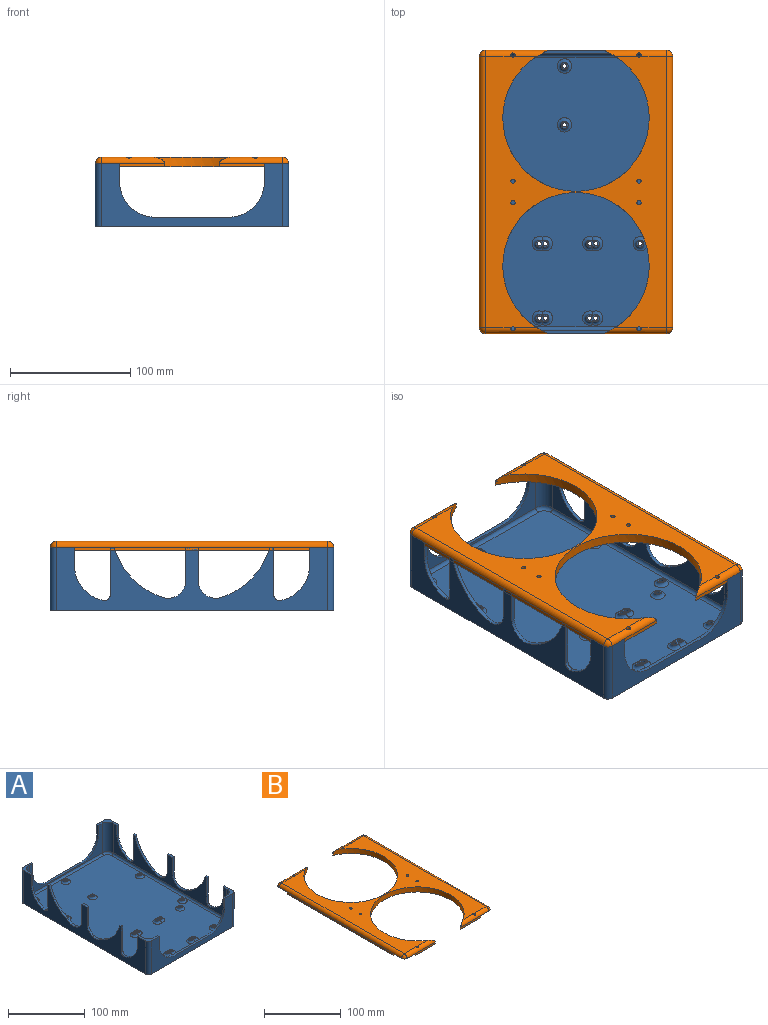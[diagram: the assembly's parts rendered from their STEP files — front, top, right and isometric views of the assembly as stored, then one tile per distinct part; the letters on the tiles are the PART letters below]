
ASSEMBLY  parts=2 mates=1
PART A: 130 faces, bbox 161x236x53 mm
  f0: plane 224x149mm, normal (0,0,1), area 31309.5mm2, adj f60,f61,f62,f63,f64,f65,f66,f67
  f1: plane 20x20mm, normal (0,0,1), area 127.1mm2, adj f5,f6,f31,f32,f35,f38,f86,f95
  f2: plane 20x20mm, normal (0,0,1), area 127.1mm2, adj f6,f7,f30,f31,f37,f40,f88,f92
  f3: plane 20x20mm, normal (0,0,1), area 127.1mm2, adj f4,f5,f29,f32,f34,f43,f84,f94
  f4: plane 151x53mm, normal (0,-1,0), area 2944.3mm2, adj f3,f28,f33,f41,f42,f43,f93,f94
  f5: plane 226x53mm, normal (1,0,0), area 5854.6mm2, adj f1,f3,f28,f34,f35,f94,f95,f101
  f6: plane 151x53mm, normal (0,1,0), area 2944.3mm2, adj f1,f2,f28,f36,f37,f38,f92,f95
  f7: plane 226x53mm, normal (-1,0,0), area 5854.6mm2, adj f2,f28,f33,f39,f40,f92,f93,f96
  f8: cylinder r=1.75mm len=6mm, axis (0,0,1), area 66mm2, adj f28,f57
  f9: cylinder r=1.75mm len=6mm, axis (0,0,1), area 66mm2, adj f28,f56
  f10: cylinder r=1.75mm len=6mm, axis (0,0,1), area 66mm2, adj f28,f59
  f11: cylinder r=1.75mm len=6mm, axis (0,0,1), area 66mm2, adj f28,f45
  f12: cylinder r=1.75mm len=6mm, axis (0,0,1), area 66mm2, adj f28,f44
  f13: cylinder r=1.75mm len=6mm, axis (0,0,1), area 66mm2, adj f28,f52
  f14: cylinder r=1.75mm len=6mm, axis (0,0,1), area 66mm2, adj f28,f51
  f15: cylinder r=1.75mm len=6mm, axis (0,0,1), area 66mm2, adj f28,f49
  f16: cylinder r=1.75mm len=6mm, axis (0,0,1), area 66mm2, adj f28,f53
  f17: cylinder r=1.75mm len=6mm, axis (0,0,1), area 66mm2, adj f28,f54
  f18: cylinder r=1.75mm len=6mm, axis (0,0,1), area 66mm2, adj f28,f58
  f19: cylinder r=1.75mm len=6mm, axis (0,0,1), area 66mm2, adj f28,f47
  f20: cylinder r=1.75mm len=6mm, axis (0,0,1), area 66mm2, adj f28,f46
  f21: cylinder r=1.75mm len=6mm, axis (0,0,1), area 66mm2, adj f28,f50
  f22: cylinder r=1.75mm len=6mm, axis (0,0,1), area 66mm2, adj f28,f48
  f23: cylinder r=1.75mm len=6mm, axis (0,0,1), area 66mm2, adj f28,f46
  f24: cylinder r=1.75mm len=6mm, axis (0,0,1), area 66mm2, adj f28,f45
  f25: cylinder r=1.75mm len=6mm, axis (0,0,1), area 66mm2, adj f28,f51
  f26: cylinder r=1.75mm len=6mm, axis (0,0,1), area 66mm2, adj f28,f50
  f27: cylinder r=1.75mm len=6mm, axis (0,0,1), area 66mm2, adj f28,f55
  f28: plane 236x161mm, normal (0,0,-1), area 37782.1mm2, adj f4,f5,f6,f7,f8,f9,f10,f11
  f29: plane 135x47mm, normal (0,1,0), area 1286.3mm2, adj f3,f33,f41,f42,f43,f80,f84,f90
  f30: plane 210x47mm, normal (1,0,0), area 3746.6mm2, adj f2,f33,f39,f40,f81,f88,f90,f96
  f31: plane 135x47mm, normal (0,-1,0), area 1286.3mm2, adj f1,f2,f36,f37,f38,f83,f86,f88
  f32: plane 210x47mm, normal (-1,0,0), area 3746.6mm2, adj f1,f3,f34,f35,f82,f84,f86,f101
  f33: plane 20x20mm, normal (0,0,1), area 127.1mm2, adj f4,f7,f29,f30,f39,f42,f90,f93
  f34: plane 15x3mm, normal (0,1,0), area 45mm2, adj f3,f5,f32,f101
  f35: plane 15x3mm, normal (0,-1,0), area 45mm2, adj f1,f5,f32,f102
  f36: plane 61x3mm, normal (0,0,1), area 183mm2, adj f6,f31,f97,f98
  f37: plane 15x3mm, normal (1,0,0), area 45mm2, adj f2,f6,f31,f98
  f38: plane 15x3mm, normal (-1,0,0), area 45mm2, adj f1,f6,f31,f97
  f39: plane 15x3mm, normal (0,1,0), area 45mm2, adj f7,f30,f33,f103
  f40: plane 15x3mm, normal (0,-1,0), area 45mm2, adj f2,f7,f30,f96
  f41: plane 61x3mm, normal (0,0,1), area 183mm2, adj f4,f29,f99,f100
  f42: plane 15x3mm, normal (1,0,0), area 45mm2, adj f4,f29,f33,f100
  f43: plane 15x3mm, normal (-1,0,0), area 45mm2, adj f3,f4,f29,f99
  f44: plane 6x6mm, normal (0,0,1), area 18.7mm2, adj f12,f67
  f45: plane 11x6mm, normal (0,0,1), area 35.1mm2, adj f11,f24,f72,f73
  f46: plane 11x6mm, normal (0,0,1), area 35.1mm2, adj f20,f23,f77,f78
  f47: plane 6x6mm, normal (0,0,1), area 18.7mm2, adj f19,f60
  f48: plane 6x6mm, normal (0,0,1), area 18.7mm2, adj f22,f70
  f49: plane 6x6mm, normal (0,0,1), area 18.7mm2, adj f15,f71
  f50: plane 11x6mm, normal (0,0,1), area 35.1mm2, adj f21,f26,f74,f75
  f51: plane 11x6mm, normal (0,0,1), area 35.1mm2, adj f14,f25,f68,f69
  f52: plane 6x6mm, normal (0,0,1), area 18.7mm2, adj f13,f76
  f53: plane 6x6mm, normal (0,0,1), area 18.7mm2, adj f16,f63
  f54: plane 6x6mm, normal (0,0,1), area 18.7mm2, adj f17,f65
  f55: plane 6x6mm, normal (0,0,1), area 18.7mm2, adj f27,f66
  f56: plane 6x6mm, normal (0,0,1), area 18.7mm2, adj f9,f64
  f57: plane 6x6mm, normal (0,0,1), area 18.7mm2, adj f8,f61
  f58: plane 6x6mm, normal (0,0,1), area 18.7mm2, adj f18,f62
  f59: plane 6x6mm, normal (0,0,1), area 18.7mm2, adj f10,f79
  f60: torus R=6mm, axis (0,0,1), area 121.1mm2, adj f0,f47
  f61: torus R=6mm, axis (0,0,1), area 116.5mm2, adj f0,f57,f62
  f62: torus R=6mm, axis (0,0,1), area 116.5mm2, adj f0,f58,f61
  f63: torus R=6mm, axis (0,0,1), area 121.1mm2, adj f0,f53
  f64: torus R=6mm, axis (0,0,1), area 121.1mm2, adj f0,f56
  f65: torus R=6mm, axis (0,0,1), area 121.1mm2, adj f0,f54
  f66: torus R=6mm, axis (0,0,1), area 121.1mm2, adj f0,f55
  f67: torus R=6mm, axis (0,0,1), area 121.1mm2, adj f0,f44
  f68: torus R=6mm, axis (0,0,1), area 86.4mm2, adj f0,f51,f69
  f69: torus R=6mm, axis (0,0,1), area 86.4mm2, adj f0,f51,f68
  f70: torus R=6mm, axis (0,0,1), area 116.5mm2, adj f0,f48,f71
  f71: torus R=6mm, axis (0,0,1), area 116.5mm2, adj f0,f49,f70
  f72: torus R=6mm, axis (0,0,1), area 86.4mm2, adj f0,f45,f73
  f73: torus R=6mm, axis (0,0,1), area 86.4mm2, adj f0,f45,f72
  f74: torus R=6mm, axis (0,0,1), area 86.4mm2, adj f0,f50,f75
  f75: torus R=6mm, axis (0,0,1), area 86.4mm2, adj f0,f50,f74
  f76: torus R=6mm, axis (0,0,1), area 121.1mm2, adj f0,f52
  f77: torus R=6mm, axis (0,0,1), area 86.4mm2, adj f0,f46,f78
  f78: torus R=6mm, axis (0,0,1), area 86.4mm2, adj f0,f46,f77
  f79: torus R=6mm, axis (0,0,1), area 121.1mm2, adj f0,f59
  f80: cylinder r=3mm len=135mm, axis (-1,0,0), area 636.2mm2, adj f0,f29,f85,f91
  f81: cylinder r=3mm len=210mm, axis (0,1,0), area 989.6mm2, adj f0,f30,f89,f91
  f82: cylinder r=3mm len=210mm, axis (0,-1,0), area 989.6mm2, adj f0,f32,f85,f87
  f83: cylinder r=3mm len=135mm, axis (1,0,0), area 636.2mm2, adj f0,f31,f87,f89
  f84: cylinder r=10mm len=47mm, axis (0,0,1), area 738.3mm2, adj f3,f29,f32,f85
  f85: torus R=7mm, axis (0,0,1), area 66mm2, adj f0,f80,f82,f84
  f86: cylinder r=10mm len=47mm, axis (0,0,-1), area 738.3mm2, adj f1,f31,f32,f87
  f87: torus R=7mm, axis (0,0,1), area 66mm2, adj f0,f82,f83,f86
  f88: cylinder r=10mm len=47mm, axis (0,0,1), area 738.3mm2, adj f2,f30,f31,f89
  f89: torus R=7mm, axis (0,0,1), area 66mm2, adj f0,f81,f83,f88
  f90: cylinder r=10mm len=47mm, axis (0,0,-1), area 738.3mm2, adj f29,f30,f33,f91
  f91: torus R=7mm, axis (0,0,1), area 66mm2, adj f0,f80,f81,f90
  f92: cylinder r=5mm len=53mm, axis (0,0,1), area 416.3mm2, adj f2,f6,f7,f28
  f93: cylinder r=5mm len=53mm, axis (0,0,-1), area 416.3mm2, adj f4,f7,f28,f33
  f94: cylinder r=5mm len=53mm, axis (0,0,1), area 416.3mm2, adj f3,f4,f5,f28
  f95: cylinder r=5mm len=53mm, axis (0,0,-1), area 416.3mm2, adj f1,f5,f6,f28
  f96: cylinder r=30mm len=29.39mm, axis (-1,0,0), area 123.2mm2, adj f7,f30,f40,f113
  f97: cylinder r=30mm len=30mm, axis (0,1,0), area 141.4mm2, adj f6,f31,f36,f38
  f98: cylinder r=30mm len=30mm, axis (0,-1,0), area 141.4mm2, adj f6,f31,f36,f37
  f99: cylinder r=30mm len=30mm, axis (0,1,0), area 141.4mm2, adj f4,f29,f41,f43
  f100: cylinder r=30mm len=30mm, axis (0,-1,0), area 141.4mm2, adj f4,f29,f41,f42
  f101: cylinder r=30mm len=29.39mm, axis (1,0,0), area 123.2mm2, adj f5,f32,f34,f126
  f102: cylinder r=30mm len=29.39mm, axis (-1,0,0), area 123.2mm2, adj f5,f32,f35,f127
  f103: cylinder r=30mm len=29.39mm, axis (1,0,0), area 123.2mm2, adj f7,f30,f39,f114
  f104: plane 3x3mm, normal (0,0,1), area 9mm2, adj f7,f30,f105,f106
  f105: plane 39.5x3mm, normal (0,1,0), area 118.5mm2, adj f7,f30,f104,f113
  f106: cylinder r=62.5mm len=41.8mm, axis (-1,0,0), area 181.1mm2, adj f7,f30,f104,f115
  f107: plane 39.5x3mm, normal (0,-1,0), area 118.5mm2, adj f7,f30,f108,f114
  f108: plane 3x3mm, normal (0,0,1), area 9mm2, adj f7,f30,f107,f109
  f109: cylinder r=62.5mm len=41.8mm, axis (-1,0,0), area 181.1mm2, adj f7,f30,f108,f116
  f110: plane 10x3mm, normal (0,0,1), area 30mm2, adj f7,f30,f111,f112
  f111: plane 27.57x3mm, normal (0,1,0), area 82.7mm2, adj f7,f30,f110,f115
  f112: plane 27.57x3mm, normal (0,-1,0), area 82.7mm2, adj f7,f30,f110,f116
  f113: cylinder r=5mm len=6mm, axis (-1,0,0), area 26.6mm2, adj f7,f30,f96,f105
  f114: cylinder r=5mm len=6mm, axis (1,0,0), area 26.6mm2, adj f7,f30,f103,f107
  f115: cylinder r=15mm len=19.74mm, axis (-1,0,0), area 85.1mm2, adj f7,f30,f106,f111
  f116: cylinder r=15mm len=19.74mm, axis (-1,0,0), area 85.1mm2, adj f7,f30,f109,f112
  f117: plane 3x3mm, normal (0,0,1), area 9mm2, adj f5,f32,f118,f119
  f118: cylinder r=62.5mm len=41.8mm, axis (1,0,0), area 181.1mm2, adj f5,f32,f117,f128
  f119: plane 39.5x3mm, normal (0,1,0), area 118.5mm2, adj f5,f32,f117,f127
  f120: plane 39.5x3mm, normal (0,-1,0), area 118.5mm2, adj f5,f32,f122,f126
  f121: cylinder r=62.5mm len=41.8mm, axis (1,0,0), area 181.1mm2, adj f5,f32,f122,f129
  f122: plane 3x3mm, normal (0,0,1), area 9mm2, adj f5,f32,f120,f121
  f123: plane 10x3mm, normal (0,0,1), area 30mm2, adj f5,f32,f124,f125
  f124: plane 27.57x3mm, normal (0,-1,0), area 82.7mm2, adj f5,f32,f123,f129
  f125: plane 27.57x3mm, normal (0,1,0), area 82.7mm2, adj f5,f32,f123,f128
  f126: cylinder r=5mm len=6mm, axis (1,0,0), area 26.6mm2, adj f5,f32,f101,f120
  f127: cylinder r=5mm len=6mm, axis (-1,0,0), area 26.6mm2, adj f5,f32,f102,f119
  f128: cylinder r=15mm len=19.74mm, axis (1,0,0), area 85.1mm2, adj f5,f32,f118,f125
  f129: cylinder r=15mm len=19.74mm, axis (1,0,0), area 85.1mm2, adj f5,f32,f121,f124
PART B: 52 faces, bbox 161x236x8 mm
  f0: plane 37.51x3mm, normal (0,1,0), area 112.5mm2, adj f17,f27,f28,f47
  f1: plane 37.51x3mm, normal (0,-1,0), area 112.5mm2, adj f24,f27,f33,f50
  f2: plane 20x20mm, normal (0,0,-1), area 127.1mm2, adj f13,f14,f15,f16,f38,f42,f43,f45
  f3: plane 20x20mm, normal (0,0,-1), area 127.1mm2, adj f17,f18,f19,f20,f39,f47,f48,f49
  f4: plane 20x20mm, normal (0,0,-1), area 127.1mm2, adj f21,f22,f23,f24,f40,f49,f50,f51
  f5: plane 196x3mm, normal (1,0,0), area 588mm2, adj f12,f13,f27,f45
  f6: plane 37.51x3mm, normal (0,1,0), area 112.5mm2, adj f16,f27,f28,f42
  f7: plane 196x3mm, normal (-1,0,0), area 588mm2, adj f20,f21,f27,f49
  f8: plane 37.51x3mm, normal (0,-1,0), area 112.5mm2, adj f25,f27,f33,f44
  f9: plane 226x151mm, normal (0,0,1), area 11543.8mm2, adj f28,f29,f30,f31,f32,f33,f34,f35
  f10: plane 20x20mm, normal (0,0,-1), area 127.1mm2, adj f11,f12,f25,f26,f41,f44,f45,f46
  f11: plane 7x3mm, normal (1,0,0), area 21mm2, adj f10,f12,f27,f41
  f12: plane 3x3mm, normal (0,-1,0), area 9mm2, adj f5,f10,f11,f27
  f13: plane 3x3mm, normal (0,1,0), area 9mm2, adj f2,f5,f14,f27
  f14: plane 7x3mm, normal (1,0,0), area 21mm2, adj f2,f13,f27,f38
  f15: plane 7x3mm, normal (0,1,0), area 21mm2, adj f2,f16,f27,f38
  f16: plane 3x3mm, normal (1,0,0), area 9mm2, adj f2,f6,f15,f27
  f17: plane 3x3mm, normal (-1,0,0), area 9mm2, adj f0,f3,f18,f27
  f18: plane 7x3mm, normal (0,1,0), area 21mm2, adj f3,f17,f27,f39
  f19: plane 7x3mm, normal (-1,0,0), area 21mm2, adj f3,f20,f27,f39
  f20: plane 3x3mm, normal (0,1,0), area 9mm2, adj f3,f7,f19,f27
  f21: plane 3x3mm, normal (0,-1,0), area 9mm2, adj f4,f7,f22,f27
  f22: plane 7x3mm, normal (-1,0,0), area 21mm2, adj f4,f21,f27,f40
  f23: plane 7x3mm, normal (0,-1,0), area 21mm2, adj f4,f24,f27,f40
  f24: plane 3x3mm, normal (-1,0,0), area 9mm2, adj f1,f4,f23,f27
  f25: plane 3x3mm, normal (1,0,0), area 9mm2, adj f8,f10,f26,f27
  f26: plane 7x3mm, normal (0,-1,0), area 21mm2, adj f10,f25,f27,f41
  f27: plane 236x161mm, normal (0,0,-1), area 14287.5mm2, adj f0,f1,f5,f6,f7,f8,f11,f12
  f28: cylinder r=61mm len=122mm, axis (0,0,1), area 2663.1mm2, adj f0,f6,f9,f27,f42,f47
  f29: cylinder r=1.75mm len=8mm, axis (0,0,1), area 85.1mm2, adj f9,f27,f50
  f30: cylinder r=1.75mm len=8mm, axis (0,0,1), area 88mm2, adj f9,f27
  f31: cylinder r=1.75mm len=8mm, axis (0,0,1), area 85.1mm2, adj f9,f27,f42
  f32: cylinder r=1.75mm len=8mm, axis (0,0,1), area 85.1mm2, adj f9,f27,f47
  f33: cylinder r=61mm len=122mm, axis (0,0,1), area 2663.1mm2, adj f1,f8,f9,f27,f44,f50
  f34: cylinder r=1.75mm len=8mm, axis (0,0,1), area 88mm2, adj f9,f27
  f35: cylinder r=1.75mm len=8mm, axis (0,0,1), area 88mm2, adj f9,f27
  f36: cylinder r=1.75mm len=8mm, axis (0,0,1), area 88mm2, adj f9,f27
  f37: cylinder r=1.75mm len=8mm, axis (0,0,1), area 85.1mm2, adj f9,f27,f44
  f38: cylinder r=10mm len=10mm, axis (0,0,-1), area 47.1mm2, adj f2,f14,f15,f27
  f39: cylinder r=10mm len=10mm, axis (0,0,1), area 47.1mm2, adj f3,f18,f19,f27
  f40: cylinder r=10mm len=10mm, axis (0,0,-1), area 47.1mm2, adj f4,f22,f23,f27
  f41: cylinder r=10mm len=10mm, axis (0,0,1), area 47.1mm2, adj f10,f11,f26,f27
  f42: cylinder r=5mm len=52.51mm, axis (1,0,0), area 373.9mm2, adj f2,f6,f9,f28,f31,f43
  f43: sphere r=5mm, area 39.3mm2, adj f2,f42,f45
  f44: cylinder r=5mm len=52.51mm, axis (-1,0,0), area 373.9mm2, adj f8,f9,f10,f33,f37,f46
  f45: cylinder r=5mm len=226mm, axis (0,-1,0), area 1775mm2, adj f2,f5,f9,f10,f43,f46
  f46: sphere r=5mm, area 39.3mm2, adj f10,f44,f45
  f47: cylinder r=5mm len=52.51mm, axis (1,0,0), area 373.9mm2, adj f0,f3,f9,f28,f32,f48
  f48: sphere r=5mm, area 39.3mm2, adj f3,f47,f49
  f49: cylinder r=5mm len=226mm, axis (0,1,0), area 1775mm2, adj f3,f4,f7,f9,f48,f51
  f50: cylinder r=5mm len=52.51mm, axis (-1,0,0), area 373.9mm2, adj f1,f4,f9,f29,f33,f51
  f51: sphere r=5mm, area 39.3mm2, adj f4,f49,f50
PLACE A t=(2.72,12.2,60.36)mm
PLACE B t=(2.72,12.2,60.36)mm
MATE fastened A.f33 <-> B.f4  axis (0,0,1) through (-47.28,-62.8,110.36)mm
